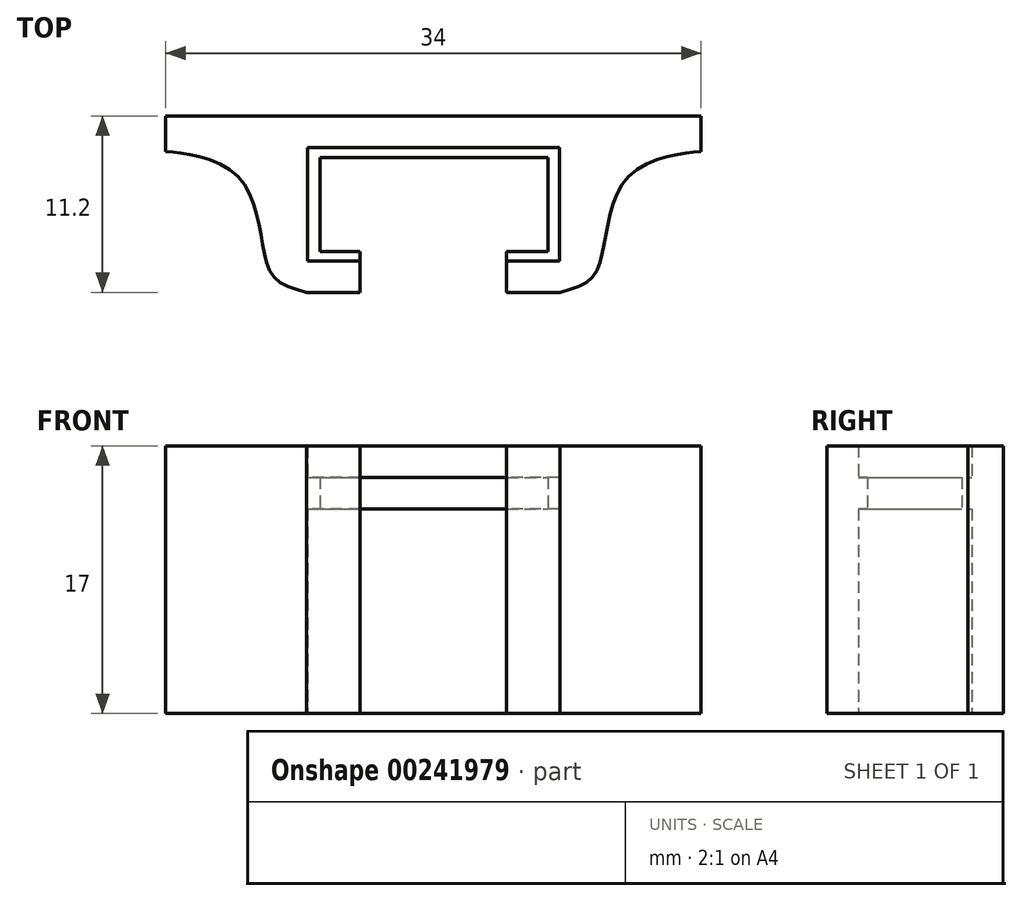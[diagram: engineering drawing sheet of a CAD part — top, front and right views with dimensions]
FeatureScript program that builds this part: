
annotation { "Feature Type Name" : "Feature", "Feature Type Description" : "" }
export const myFeature = defineFeature(function(context is Context, id is Id, definition is map)
    precondition{}
    {
        {
            var Q0;
            Q0=qCreatedBy(makeId("Top.planeOp"),FACE);
            var sketch = newSketch(context, id + "F0", { "sketchPlane" : qUnion([Q0])});
            skLineSegment(sketch, "E0.bottom", {"start": v(8, -3.6) * mm, "end": v(4.65, -3.6) * mm});
            skLineSegment(sketch, "E0.top", {"start": v(8, 3.6) * mm, "end": v(-8, 3.6) * mm});
            skLineSegment(sketch, "E0.left", {"start": v(8, -3.6) * mm, "end": v(8, 3.6) * mm});
            skLineSegment(sketch, "E0.right", {"start": v(-8, -3.6) * mm, "end": v(-8, 3.6) * mm});
            skPoint(sketch, "E0.middle", {"position": v(0, 0) * mm});
            skLineSegment(sketch, "E1.1", {"start": v(10, 5.6) * mm, "end": v(-10, 5.6) * mm});
            skLineSegment(sketch, "E2.bottom", {"start": v(-7.2, -3.6) * mm, "end": v(-4.65, -3.6) * mm});
            skLineSegment(sketch, "E2.top", {"start": v(-7.2, 2.97) * mm, "end": v(7.27, 2.97) * mm});
            skLineSegment(sketch, "E2.left", {"start": v(-7.2, -3.02) * mm, "end": v(-7.2, 2.97) * mm});
            skLineSegment(sketch, "E2.right", {"start": v(7.27, -3.02) * mm, "end": v(7.27, 2.97) * mm});
            skLineSegment(sketch, "E3.bottom", {"start": v(-8, -3.6) * mm, "end": v(-4.65, -3.6) * mm});
            skLineSegment(sketch, "E3.top", {"start": v(-10, -5.6) * mm, "end": v(-4.65, -5.6) * mm});
            skLineSegment(sketch, "E4", {"start": v(-7.2, -3.02) * mm, "end": v(-4.65, -3.02) * mm});
            skLineSegment(sketch, "E5.left", {"start": v(4.65, -3.02) * mm, "end": v(4.65, -5.6) * mm});
            skLineSegment(sketch, "E5.right", {"start": v(-4.65, -3.02) * mm, "end": v(-4.65, -5.6) * mm});
            skPoint(sketch, "E5.middle", {"position": v(0, -5.6) * mm});
            skPoint(sketch, "E6.orphan", {"position": v(-4.65, -2.63) * mm});
            skPoint(sketch, "E7.orphan", {"position": v(4.65, -2.63) * mm});
            skLineSegment(sketch, "E8.trimOffspring", {"start": v(4.65, -3.02) * mm, "end": v(7.27, -3.02) * mm});
            skLineSegment(sketch, "E9.trimOffspring", {"start": v(4.65, -3.6) * mm, "end": v(7.27, -3.6) * mm});
            skLineSegment(sketch, "E10.trimOffspring", {"start": v(-4.65, -3.6) * mm, "end": v(-8, -3.6) * mm});
            skLineSegment(sketch, "E11.trimOffspring", {"start": v(4.65, -3.6) * mm, "end": v(8, -3.6) * mm});
            skLineSegment(sketch, "E12.trimOffspring", {"start": v(4.65, -5.6) * mm, "end": v(10, -5.6) * mm});
            skPoint(sketch, "E5.top.end.orphan", {"position": v(-4.65, -8.57) * mm});
            skPoint(sketch, "E5.top.start.orphan", {"position": v(4.65, -8.57) * mm});
            skLineSegment(sketch, "E13.bottom", {"start": v(17, 5.6) * mm, "end": v(-17, 5.6) * mm});
            skLineSegment(sketch, "E13.top", {"start": v(10, -5.6) * mm, "end": v(4.65, -5.6) * mm});
            skLineSegment(sketch, "E13.left", {"start": v(17, 5.6) * mm, "end": v(17, -5.6) * mm});
            skLineSegment(sketch, "E13.right", {"start": v(-17, 5.6) * mm, "end": v(-17, -5.6) * mm});
            skLineSegment(sketch, "E14.trimOffspring", {"start": v(-4.65, -5.6) * mm, "end": v(-17, -5.6) * mm});
            skPoint(sketch, "E1.2.start.orphan", {"position": v(10, -3.6) * mm});
            skLineSegment(sketch, "E15", {"start": v(10, -5.6) * mm, "end": v(17, -5.6) * mm});
            skFitSpline(sketch, "E16", {"points": [v(17, 3.36) * mm, v(15.34, 3.13) * mm, v(12.59, 1.94) * mm, v(11.25, -0.59) * mm, v(10.72, -3.12) * mm, v(10, -4.76) * mm, v(8.04, -5.6) * mm], "startDerivative": vector(-10.66, -0.93) * mm, "endDerivative": vector(-14.09, -3.82) * mm});
            skFitSpline(sketch, "E17.MirrorCS", {"points": [v(-17, 3.36) * mm, v(-15.34, 3.13) * mm, v(-12.59, 1.94) * mm, v(-11.25, -0.59) * mm, v(-10.72, -3.12) * mm, v(-10, -4.76) * mm, v(-8.04, -5.6) * mm], "startDerivative": vector(10.66, -0.93) * mm, "endDerivative": vector(14.09, -3.82) * mm});
            skSolve(sketch);
        }
        {
            var Q0;
            Q0=makeQuery(id+"F0.imprint","IMPRINT",FACE,{"disambiguationData":[TD([[makeQuery(id+"F0.imprint","IMPRINT",EDGE,{"derivedFrom":sQuery(id+"F0.wireOp",EDGE,"E0.top")}),1.0]])]});
            extrude(context, id + "F1", {"entities" : qUnion([Q0]), "depth" : 2 * mm});
        }
        {
            var Q0;
            Q0=makeQuery(id+"F0.imprint","IMPRINT",FACE,{"disambiguationData":[TD([[makeQuery(id+"F0.imprint","IMPRINT",EDGE,{"derivedFrom":sQuery(id+"F0.wireOp",EDGE,"E0.top")}),-1.0]])]});
            extrude(context, id + "F2", {"entities" : qUnion([Q0]), "operationType" : NewBodyOperationType.ADD, "depth" : 4 * mm, "hasSecondDirection" : true, "secondDirectionOppositeDirection" : true, "secondDirectionDepth" : 13 * mm});
        }
    });
